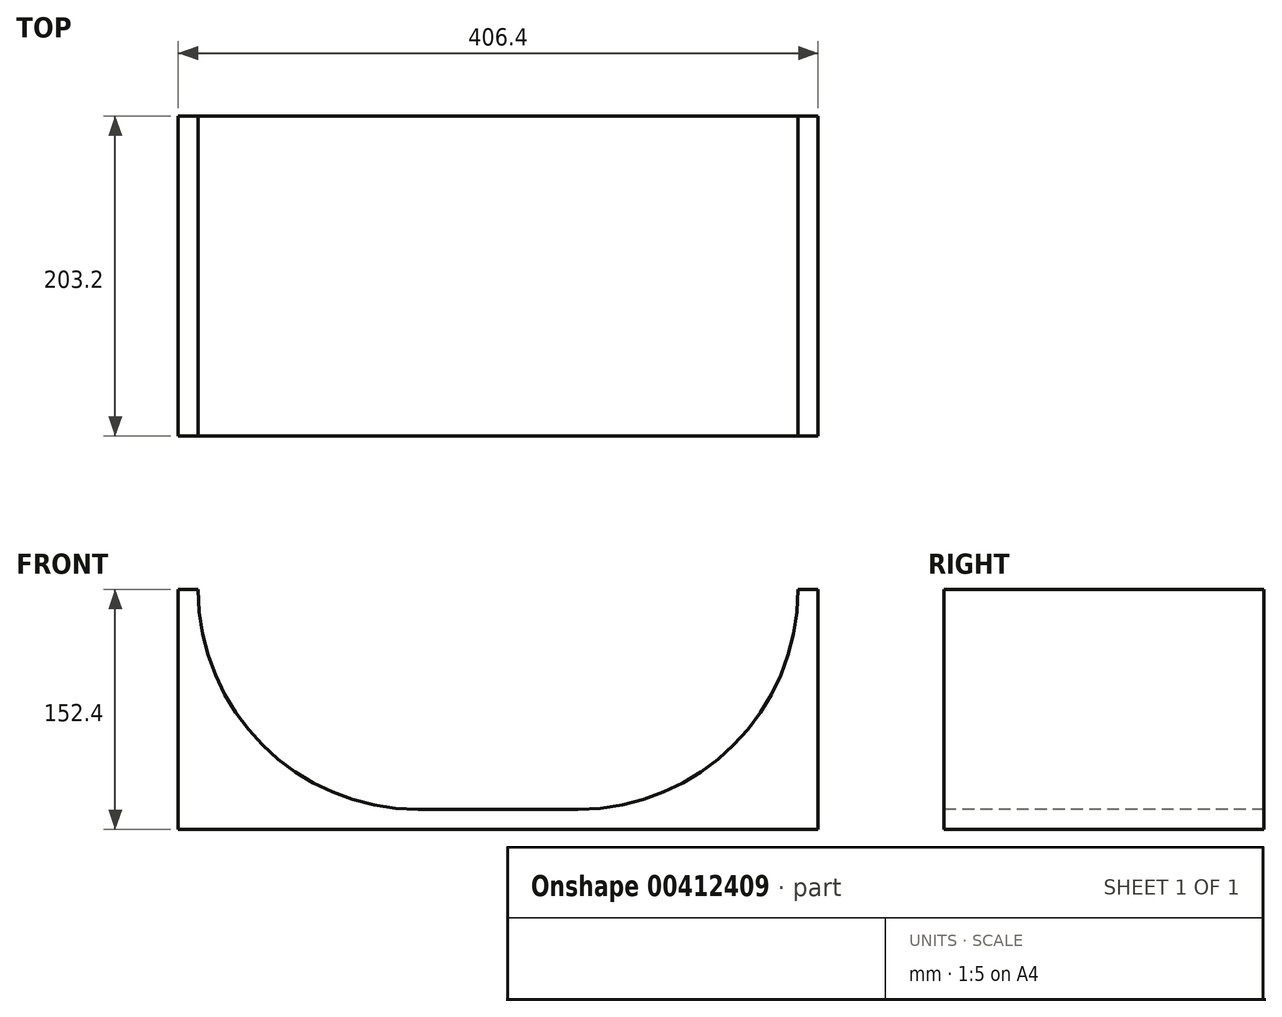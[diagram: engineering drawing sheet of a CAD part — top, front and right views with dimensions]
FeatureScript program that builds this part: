
annotation { "Feature Type Name" : "Feature", "Feature Type Description" : "" }
export const myFeature = defineFeature(function(context is Context, id is Id, definition is map)
    precondition{}
    {
        {
            var Q0;
            Q0=qCreatedBy(makeId("Top.planeOp"),FACE);
            var sketch = newSketch(context, id + "F0", { "sketchPlane" : qUnion([Q0])});
            skLineSegment(sketch, "E0.bottom", {"start": v(0, 0) * mm, "end": v(-50.8, 0) * mm});
            skLineSegment(sketch, "E0.top", {"start": v(0, 101.6) * mm, "end": v(-50.8, 101.6) * mm});
            skLineSegment(sketch, "E0.left", {"start": v(0, 0) * mm, "end": v(0, 101.6) * mm});
            skLineSegment(sketch, "E0.right", {"start": v(-50.8, 0) * mm, "end": v(-50.8, 101.6) * mm});
            skLineSegment(sketch, "E1.bottom", {"start": v(-50.8, 101.6) * mm, "end": v(-203.2, 101.6) * mm});
            skLineSegment(sketch, "E1.top", {"start": v(-50.8, 0) * mm, "end": v(-203.2, 0) * mm});
            skLineSegment(sketch, "E1.left", {"start": v(-50.8, 101.6) * mm, "end": v(-50.8, 0) * mm});
            skLineSegment(sketch, "E1.right", {"start": v(-203.2, 101.6) * mm, "end": v(-203.2, 0) * mm});
            skSolve(sketch);
        }
        {
            var Q0;
            Q0=makeQuery(id+"F0.imprint","IMPRINT",FACE,{"disambiguationData":[TD([[makeQuery(id+"F0.imprint","IMPRINT",EDGE,{"derivedFrom":sQuery(id+"F0.wireOp",EDGE,"E1.bottom")}),1.0]])]});
            extrude(context, id + "F1", {"entities" : qUnion([Q0]), "depth" : 152.4 * mm});
        }
        {
            var Q0;
            Q0=makeQuery(id+"F1.opExtrude","SWEPT_FACE",FACE,{"disambiguationData":[OSD([sQuery(id+"F0.wireOp",EDGE,"E1.top")])]});
            var sketch = newSketch(context, id + "F2", { "sketchPlane" : qUnion([Q0])});
            skPoint(sketch, "E2", {"position": v(-50.8, 152.4) * mm});
            skSolve(sketch);
        }
        {
            var Q0;
            Q0=sQuery(id+"F2.wireOp",VERTEX,"E2");
            var Q1;
            Q1=makeQuery(id+"F1.opExtrude","SWEPT_BODY",BODY,{"disambiguationData":[OSD([sQuery(id+"F0.wireOp",EDGE,"E1.bottom"),sQuery(id+"F0.wireOp",EDGE,"E1.top"),sQuery(id+"F0.wireOp",EDGE,"E1.left"),sQuery(id+"F0.wireOp",EDGE,"E1.right")])]});
            hole(context, id + "F3", {"style" : HoleStyle.SIMPLE, "endStyle" : HoleEndStyle.THROUGH, "holeDiameter" : 279.4 * mm, "isTappedThrough" : true, "tappedDepth" : 12.7 * mm, "tapClearance" : 3, "locations" : qUnion([Q0]), "scope" : qUnion([Q1])});
        }
        {
            var Q0;
            Q0=makeQuery(id+"F0.imprint","IMPRINT",FACE,{"disambiguationData":[TD([[makeQuery(id+"F0.imprint","IMPRINT",EDGE,{"derivedFrom":sQuery(id+"F0.wireOp",EDGE,"E0.bottom")}),-1.0]])]});
            extrude(context, id + "F4", {"entities" : qUnion([Q0]), "operationType" : NewBodyOperationType.ADD, "depth" : 12.7 * mm});
        }
        {
            var Q0;
            Q0=makeQuery(id+"F1.opExtrude","SWEPT_BODY",BODY,{"disambiguationData":[OSD([sQuery(id+"F0.wireOp",EDGE,"E1.bottom"),sQuery(id+"F0.wireOp",EDGE,"E1.top"),sQuery(id+"F0.wireOp",EDGE,"E1.left"),sQuery(id+"F0.wireOp",EDGE,"E1.right")])]});
            var Q1;
            Q1=qCreatedBy(makeId("Front.planeOp"),FACE);
            mirror(context, id + "F5", {"operationType" : NewBodyOperationType.ADD, "entities" : qUnion([Q0]), "mirrorPlane" : qUnion([Q1])});
        }
        {
            var Q0;
            Q0=makeQuery(id+"F1.opExtrude","SWEPT_BODY",BODY,{"disambiguationData":[OSD([sQuery(id+"F0.wireOp",EDGE,"E1.bottom"),sQuery(id+"F0.wireOp",EDGE,"E1.top"),sQuery(id+"F0.wireOp",EDGE,"E1.left"),sQuery(id+"F0.wireOp",EDGE,"E1.right")])]});
            var Q1;
            Q1=qCreatedBy(makeId("Right.planeOp"),FACE);
            mirror(context, id + "F6", {"operationType" : NewBodyOperationType.ADD, "entities" : qUnion([Q0]), "mirrorPlane" : qUnion([Q1])});
        }
    });
